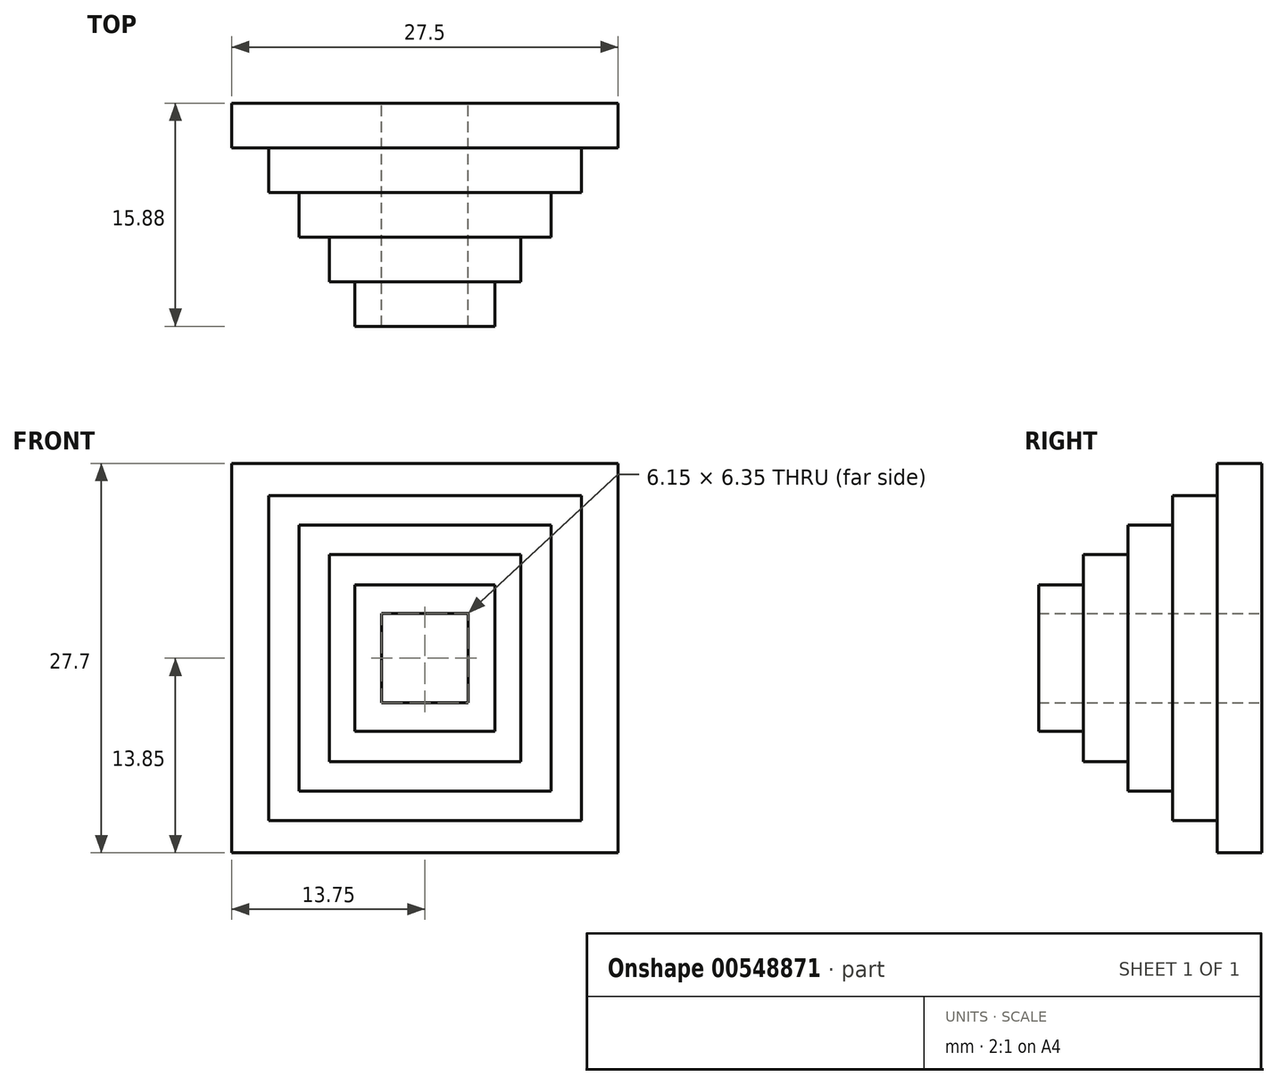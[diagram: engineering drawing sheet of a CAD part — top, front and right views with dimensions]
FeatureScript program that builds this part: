
annotation { "Feature Type Name" : "Feature", "Feature Type Description" : "" }
export const myFeature = defineFeature(function(context is Context, id is Id, definition is map)
    precondition{}
    {
        {
            var Q0;
            Q0=qCreatedBy(makeId("Front.planeOp"),FACE);
            var sketch = newSketch(context, id + "F0", { "sketchPlane" : qUnion([Q0])});
            skLineSegment(sketch, "E0.bottom", {"start": v(16.17, 16.14) * mm, "end": v(-16.17, 16.14) * mm});
            skLineSegment(sketch, "E0.top", {"start": v(16.17, -16.14) * mm, "end": v(-16.17, -16.14) * mm});
            skLineSegment(sketch, "E0.left", {"start": v(16.17, 16.14) * mm, "end": v(16.17, -16.14) * mm});
            skLineSegment(sketch, "E0.right", {"start": v(-16.17, 16.14) * mm, "end": v(-16.17, -16.14) * mm});
            skPoint(sketch, "E0.middle", {"position": v(0, 0) * mm});
            skLineSegment(sketch, "E1.bottom", {"start": v(13.75, 13.85) * mm, "end": v(-13.75, 13.85) * mm});
            skLineSegment(sketch, "E1.top", {"start": v(13.75, -13.85) * mm, "end": v(-13.75, -13.85) * mm});
            skLineSegment(sketch, "E1.left", {"start": v(13.75, 13.85) * mm, "end": v(13.75, -13.85) * mm});
            skLineSegment(sketch, "E1.right", {"start": v(-13.75, 13.85) * mm, "end": v(-13.75, -13.85) * mm});
            skLineSegment(sketch, "E2.bottom", {"start": v(11.13, 11.55) * mm, "end": v(-11.13, 11.55) * mm});
            skLineSegment(sketch, "E2.top", {"start": v(11.13, -11.55) * mm, "end": v(-11.13, -11.55) * mm});
            skLineSegment(sketch, "E2.left", {"start": v(11.13, 11.55) * mm, "end": v(11.13, -11.55) * mm});
            skLineSegment(sketch, "E2.right", {"start": v(-11.13, 11.55) * mm, "end": v(-11.13, -11.55) * mm});
            skLineSegment(sketch, "E3.bottom", {"start": v(8.97, 9.46) * mm, "end": v(-8.97, 9.46) * mm});
            skLineSegment(sketch, "E3.top", {"start": v(8.97, -9.46) * mm, "end": v(-8.97, -9.46) * mm});
            skLineSegment(sketch, "E3.left", {"start": v(8.97, 9.46) * mm, "end": v(8.97, -9.46) * mm});
            skLineSegment(sketch, "E3.right", {"start": v(-8.97, 9.46) * mm, "end": v(-8.97, -9.46) * mm});
            skLineSegment(sketch, "E4.bottom", {"start": v(6.8, 7.36) * mm, "end": v(-6.8, 7.36) * mm});
            skLineSegment(sketch, "E4.top", {"start": v(6.8, -7.36) * mm, "end": v(-6.8, -7.36) * mm});
            skLineSegment(sketch, "E4.left", {"start": v(6.8, 7.36) * mm, "end": v(6.8, -7.36) * mm});
            skLineSegment(sketch, "E4.right", {"start": v(-6.8, 7.36) * mm, "end": v(-6.8, -7.36) * mm});
            skLineSegment(sketch, "E5.bottom", {"start": v(4.98, 5.2) * mm, "end": v(-4.98, 5.2) * mm});
            skLineSegment(sketch, "E5.top", {"start": v(4.98, -5.2) * mm, "end": v(-4.98, -5.2) * mm});
            skLineSegment(sketch, "E5.left", {"start": v(4.98, 5.2) * mm, "end": v(4.98, -5.2) * mm});
            skLineSegment(sketch, "E5.right", {"start": v(-4.98, 5.2) * mm, "end": v(-4.98, -5.2) * mm});
            skLineSegment(sketch, "E6.bottom", {"start": v(3.08, 3.18) * mm, "end": v(-3.08, 3.18) * mm});
            skLineSegment(sketch, "E6.top", {"start": v(3.08, -3.18) * mm, "end": v(-3.08, -3.18) * mm});
            skLineSegment(sketch, "E6.left", {"start": v(3.08, 3.18) * mm, "end": v(3.08, -3.18) * mm});
            skLineSegment(sketch, "E6.right", {"start": v(-3.08, 3.18) * mm, "end": v(-3.08, -3.18) * mm});
            skSolve(sketch);
        }
        {
            var Q0;
            Q0=makeQuery(id+"F0.imprint","IMPRINT",FACE,{"disambiguationData":[TD([[makeQuery(id+"F0.imprint","IMPRINT",EDGE,{"derivedFrom":sQuery(id+"F0.wireOp",EDGE,"E1.bottom")}),1.0]])]});
            extrude(context, id + "F1", {"entities" : qUnion([Q0]), "depth" : 3.17 * mm, "offsetDistance" : 25.4 * mm});
        }
        {
            var Q0;
            Q0=makeQuery(id+"F0.imprint","IMPRINT",FACE,{"disambiguationData":[TD([[makeQuery(id+"F0.imprint","IMPRINT",EDGE,{"derivedFrom":sQuery(id+"F0.wireOp",EDGE,"E2.bottom")}),1.0]])]});
            extrude(context, id + "F2", {"entities" : qUnion([Q0]), "operationType" : NewBodyOperationType.ADD, "depth" : 6.35 * mm, "offsetDistance" : 25.4 * mm});
        }
        {
            var Q0;
            Q0=makeQuery(id+"F0.imprint","IMPRINT",FACE,{"disambiguationData":[TD([[makeQuery(id+"F0.imprint","IMPRINT",EDGE,{"derivedFrom":sQuery(id+"F0.wireOp",EDGE,"E3.bottom")}),1.0]])]});
            extrude(context, id + "F3", {"entities" : qUnion([Q0]), "operationType" : NewBodyOperationType.ADD, "depth" : 9.52 * mm, "offsetDistance" : 25.4 * mm});
        }
        {
            var Q0;
            Q0=makeQuery(id+"F0.imprint","IMPRINT",FACE,{"disambiguationData":[TD([[makeQuery(id+"F0.imprint","IMPRINT",EDGE,{"derivedFrom":sQuery(id+"F0.wireOp",EDGE,"E4.bottom")}),1.0]])]});
            extrude(context, id + "F4", {"entities" : qUnion([Q0]), "operationType" : NewBodyOperationType.ADD, "depth" : 12.7 * mm, "offsetDistance" : 25.4 * mm});
        }
        {
            var Q0;
            Q0=makeQuery(id+"F0.imprint","IMPRINT",FACE,{"disambiguationData":[TD([[makeQuery(id+"F0.imprint","IMPRINT",EDGE,{"derivedFrom":sQuery(id+"F0.wireOp",EDGE,"E5.bottom")}),1.0]])]});
            extrude(context, id + "F5", {"entities" : qUnion([Q0]), "operationType" : NewBodyOperationType.ADD, "depth" : 15.88 * mm, "offsetDistance" : 25.4 * mm});
        }
    });
